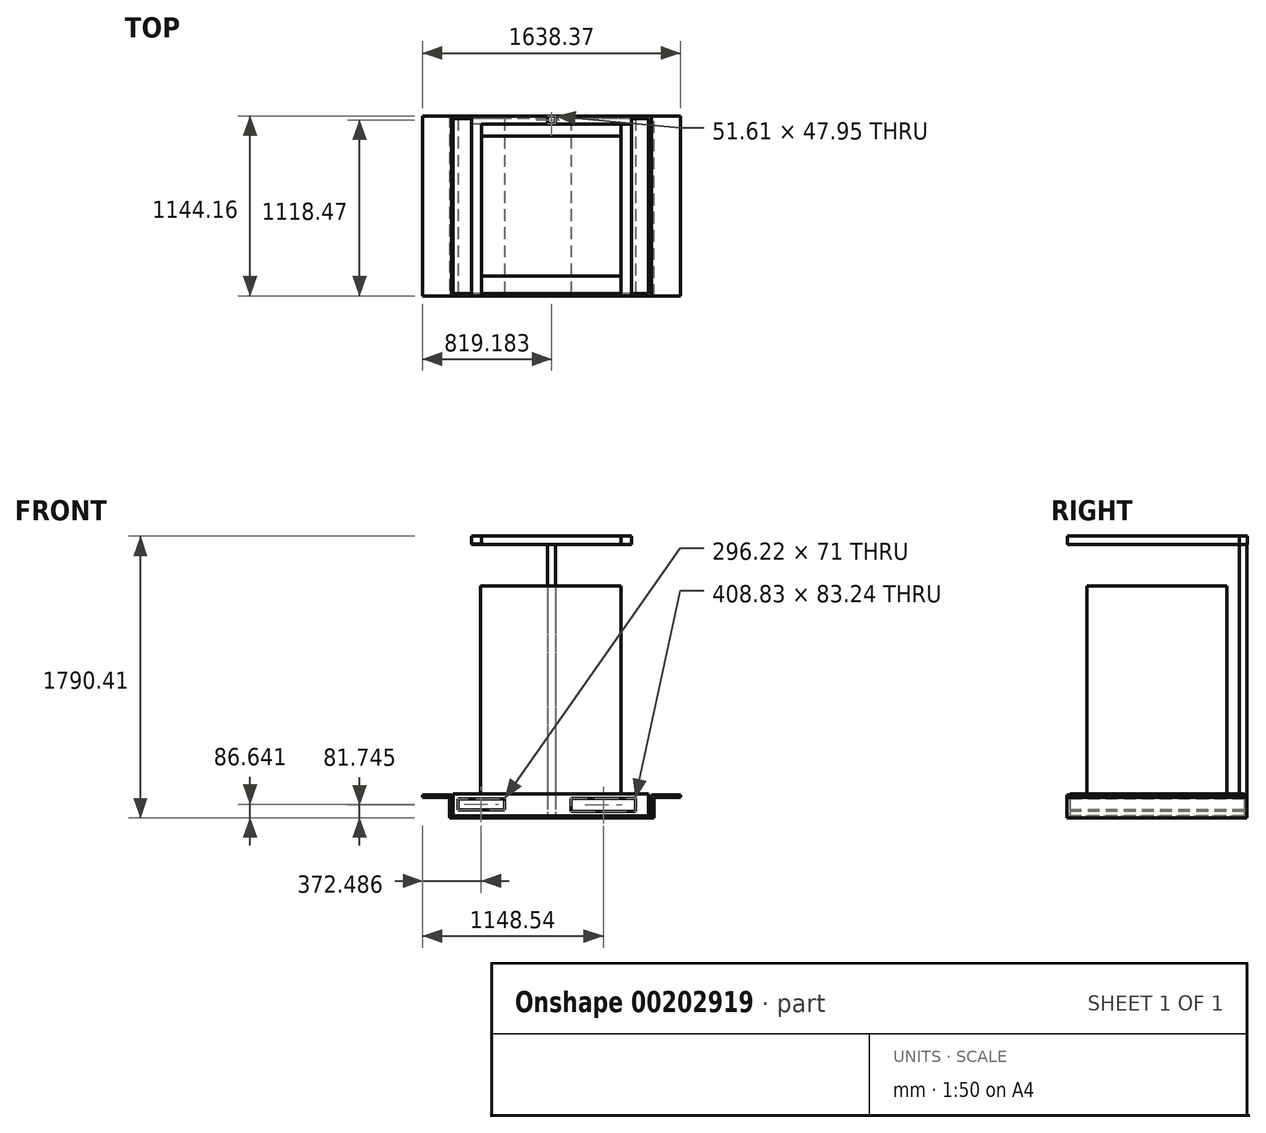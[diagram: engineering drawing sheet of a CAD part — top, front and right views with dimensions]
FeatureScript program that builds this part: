
annotation { "Feature Type Name" : "Feature", "Feature Type Description" : "" }
export const myFeature = defineFeature(function(context is Context, id is Id, definition is map)
    precondition{}
    {
        {
            var Q0;
            Q0=qCreatedBy(makeId("Front.planeOp"),FACE);
            var sketch = newSketch(context, id + "F0", { "sketchPlane" : qUnion([Q0])});
            skLineSegment(sketch, "E0.bottom", {"start": v(-65.9, -40.87) * mm, "end": v(1218.93, -40.87) * mm});
            skLineSegment(sketch, "E0.top", {"start": v(-65.9, -53.28) * mm, "end": v(1218.93, -53.28) * mm});
            skLineSegment(sketch, "E0.left", {"start": v(-65.9, -40.87) * mm, "end": v(-65.9, -53.28) * mm});
            skLineSegment(sketch, "E0.right", {"start": v(1218.93, -40.87) * mm, "end": v(1218.93, -53.28) * mm});
            skSolve(sketch);
        }
        {
            var Q0;
            Q0 = qSketchRegion(id + "F0", true);
            extrude(context, id + "F1", {"entities" : qUnion([Q0]), "endBound" : BoundingType.SYMMETRIC, "depth" : 1143 * mm});
        }
        {
            var Q0;
            Q0=makeQuery(id+"F1.opExtrude","CAP_FACE",FACE,{"disambiguationData":[OSD([sQuery(id+"F0.wireOp",EDGE,"E0.bottom"),sQuery(id+"F0.wireOp",EDGE,"E0.top"),sQuery(id+"F0.wireOp",EDGE,"E0.left"),sQuery(id+"F0.wireOp",EDGE,"E0.right")])],"isStart":false});
            var sketch = newSketch(context, id + "F2", { "sketchPlane" : qUnion([Q0])});
            skLineSegment(sketch, "E1", {"start": v(-65.9, -40.87) * mm, "end": v(-65.9, 93.39) * mm});
            skLineSegment(sketch, "E2", {"start": v(-65.9, 93.39) * mm, "end": v(-249.8, 93.39) * mm});
            skLineSegment(sketch, "E3", {"start": v(-249.8, 93.39) * mm, "end": v(-249.8, 77.85) * mm});
            skLineSegment(sketch, "E4", {"start": v(-65.9, -40.87) * mm, "end": v(-65.9, -53.28) * mm});
            skLineSegment(sketch, "E5", {"start": v(-65.9, -53.28) * mm, "end": v(-80.16, -53.28) * mm});
            skLineSegment(sketch, "E6", {"start": v(-80.16, -53.28) * mm, "end": v(-80.16, 77.85) * mm});
            skLineSegment(sketch, "E7", {"start": v(-249.8, 77.85) * mm, "end": v(-80.16, 77.85) * mm});
            skSolve(sketch);
        }
        {
            var Q0;
            Q0 = qSketchRegion(id + "F2", true);
            extrude(context, id + "F3", {"entities" : qUnion([Q0]), "operationType" : NewBodyOperationType.ADD, "oppositeDirection" : true, "depth" : 1143 * mm});
        }
        {
            var Q0;
            Q0=makeQuery(id+"F3.opExtrude","SWEPT_FACE",FACE,{"disambiguationData":[OSD([sQuery(id+"F2.wireOp",EDGE,"E6")])]});
            var Q1;
            Q1=makeQuery(id+"F1.opExtrude","SWEPT_FACE",FACE,{"disambiguationData":[OSD([sQuery(id+"F0.wireOp",EDGE,"E0.right")])]});
            cPlane(context, id + "F4", {"entities" : qUnion([Q0, Q1]), "cplaneType" : CPlaneType.MID_PLANE, "offset" : 25.4 * mm, "width" : 152.4 * mm, "height" : 152.4 * mm});
        }
        {
            var Q0;
            Q0=makeQuery(id+"F1.opExtrude","SWEPT_BODY",BODY,{"disambiguationData":[OSD([sQuery(id+"F0.wireOp",EDGE,"E0.bottom"),sQuery(id+"F0.wireOp",EDGE,"E0.top"),sQuery(id+"F0.wireOp",EDGE,"E0.left"),sQuery(id+"F0.wireOp",EDGE,"E0.right")])]});
            var Q1;
            Q1=qCreatedBy(id+"F4.planeOp",FACE);
            mirror(context, id + "F5", {"operationType" : NewBodyOperationType.ADD, "entities" : qUnion([Q0]), "mirrorPlane" : qUnion([Q1])});
        }
        {
            var Q0;
            Q0=makeQuery(id+"F1.opExtrude","SWEPT_FACE",FACE,{"disambiguationData":[OSD([sQuery(id+"F0.wireOp",EDGE,"E0.bottom")])]});
            var sketch = newSketch(context, id + "F6", { "sketchPlane" : qUnion([Q0])});
            skLineSegment(sketch, "E8.bottom", {"start": v(595.19, 570.95) * mm, "end": v(543.58, 570.95) * mm});
            skLineSegment(sketch, "E8.top", {"start": v(595.19, 523) * mm, "end": v(543.58, 523) * mm});
            skLineSegment(sketch, "E8.left", {"start": v(595.19, 570.95) * mm, "end": v(595.19, 523) * mm});
            skLineSegment(sketch, "E8.right", {"start": v(543.58, 570.95) * mm, "end": v(543.58, 523) * mm});
            skPoint(sketch, "E8.middle", {"position": v(569.38, 546.97) * mm});
            skSolve(sketch);
        }
        {
            var Q0;
            Q0 = qSketchRegion(id + "F6", true);
            extrude(context, id + "F7", {"entities" : qUnion([Q0]), "operationType" : NewBodyOperationType.ADD, "depth" : 1778 * mm});
        }
        {
            var Q0;
            Q0=qCreatedBy(id+"F4.planeOp",FACE);
            var sketch = newSketch(context, id + "F8", { "sketchPlane" : qUnion([Q0])});
            skLineSegment(sketch, "E9.bottom", {"start": v(-572.66, 1736.65) * mm, "end": v(-521.2, 1736.65) * mm});
            skLineSegment(sketch, "E9.top", {"start": v(-572.66, 1685.18) * mm, "end": v(-521.2, 1685.18) * mm});
            skLineSegment(sketch, "E9.left", {"start": v(-572.66, 1736.65) * mm, "end": v(-572.66, 1685.18) * mm});
            skLineSegment(sketch, "E9.right", {"start": v(-521.2, 1736.65) * mm, "end": v(-521.2, 1685.18) * mm});
            skPoint(sketch, "E9.middle", {"position": v(-546.93, 1710.91) * mm});
            skSolve(sketch);
        }
        {
            var Q0;
            Q0 = qSketchRegion(id + "F8", true);
            extrude(context, id + "F9", {"entities" : qUnion([Q0]), "operationType" : NewBodyOperationType.ADD, "endBound" : BoundingType.SYMMETRIC, "depth" : 1016 * mm});
        }
        {
            var Q0;
            Q0=makeQuery(id+"F9.opExtrude","SWEPT_FACE",FACE,{"disambiguationData":[OSD([sQuery(id+"F8.wireOp",EDGE,"E9.right")])]});
            var sketch = newSketch(context, id + "F10", { "sketchPlane" : qUnion([Q0])});
            skLineSegment(sketch, "E10.bottom", {"start": v(125.13, 1736.65) * mm, "end": v(61.48, 1736.65) * mm});
            skLineSegment(sketch, "E10.top", {"start": v(125.13, 1685.74) * mm, "end": v(61.48, 1685.74) * mm});
            skLineSegment(sketch, "E10.left", {"start": v(125.13, 1736.65) * mm, "end": v(125.13, 1685.74) * mm});
            skLineSegment(sketch, "E10.right", {"start": v(61.48, 1736.65) * mm, "end": v(61.48, 1685.74) * mm});
            skLineSegment(sketch, "E11.bottom", {"start": v(1076.3, 1736.46) * mm, "end": v(1010.24, 1736.46) * mm});
            skLineSegment(sketch, "E11.top", {"start": v(1076.3, 1684.97) * mm, "end": v(1010.24, 1684.97) * mm});
            skLineSegment(sketch, "E11.left", {"start": v(1076.3, 1736.46) * mm, "end": v(1076.3, 1684.97) * mm});
            skLineSegment(sketch, "E11.right", {"start": v(1010.24, 1736.46) * mm, "end": v(1010.24, 1684.97) * mm});
            skPoint(sketch, "E11.middle", {"position": v(1043.28, 1710.71) * mm});
            skSolve(sketch);
        }
        {
            var Q0;
            Q0 = qSketchRegion(id + "F10", true);
            extrude(context, id + "F11", {"entities" : qUnion([Q0]), "operationType" : NewBodyOperationType.ADD, "depth" : 1092.2 * mm});
        }
        {
            var Q0;
            Q0=makeQuery(id+"F1.opExtrude","SWEPT_FACE",FACE,{"disambiguationData":[OSD([sQuery(id+"F0.wireOp",EDGE,"E0.bottom")])]});
            var sketch = newSketch(context, id + "F12", { "sketchPlane" : qUnion([Q0])});
            skLineSegment(sketch, "E12.bottom", {"start": v(1185.44, 554.6) * mm, "end": v(-56.5, 554.6) * mm});
            skLineSegment(sketch, "E12.top", {"start": v(1185.44, -554.6) * mm, "end": v(-56.5, -554.6) * mm});
            skLineSegment(sketch, "E12.left", {"start": v(1185.44, 554.6) * mm, "end": v(1185.44, -554.6) * mm});
            skLineSegment(sketch, "E12.right", {"start": v(-56.5, 554.6) * mm, "end": v(-56.5, -554.6) * mm});
            skPoint(sketch, "E12.middle", {"position": v(564.47, 0) * mm});
            skSolve(sketch);
        }
        {
            var Q0;
            Q0 = qSketchRegion(id + "F12", true);
            extrude(context, id + "F13", {"entities" : qUnion([Q0]), "operationType" : NewBodyOperationType.ADD, "depth" : 139.7 * mm});
        }
        {
            var Q0;
            Q0=makeQuery(id+"F13.opExtrude","SWEPT_FACE",FACE,{"disambiguationData":[OSD([sQuery(id+"F12.wireOp",EDGE,"E12.top")])]});
            var sketch = newSketch(context, id + "F14", { "sketchPlane" : qUnion([Q0])});
            skLineSegment(sketch, "E13.bottom", {"start": v(270.8, 68.86) * mm, "end": v(-25.42, 68.86) * mm});
            skLineSegment(sketch, "E13.top", {"start": v(270.8, -2.14) * mm, "end": v(-25.42, -2.14) * mm});
            skLineSegment(sketch, "E13.left", {"start": v(270.8, 68.86) * mm, "end": v(270.8, -2.14) * mm});
            skLineSegment(sketch, "E13.right", {"start": v(-25.42, 68.86) * mm, "end": v(-25.42, -2.14) * mm});
            skPoint(sketch, "E13.middle", {"position": v(122.69, 33.36) * mm});
            skLineSegment(sketch, "E14.bottom", {"start": v(1103.15, 70.08) * mm, "end": v(694.32, 70.08) * mm});
            skLineSegment(sketch, "E14.top", {"start": v(1103.15, -13.15) * mm, "end": v(694.32, -13.15) * mm});
            skLineSegment(sketch, "E14.left", {"start": v(1103.15, 70.08) * mm, "end": v(1103.15, -13.15) * mm});
            skLineSegment(sketch, "E14.right", {"start": v(694.32, 70.08) * mm, "end": v(694.32, -13.15) * mm});
            skPoint(sketch, "E14.middle", {"position": v(898.73, 28.46) * mm});
            skSolve(sketch);
        }
        {
            var Q0;
            Q0 = qSketchRegion(id + "F14", true);
            extrude(context, id + "F15", {"entities" : qUnion([Q0]), "operationType" : NewBodyOperationType.REMOVE, "endBound" : BoundingType.THROUGH_ALL, "oppositeDirection" : true, "depth" : 25.4 * mm});
        }
        {
            var Q0;
            Q0=makeQuery(id+"F13.opExtrude","CAP_FACE",FACE,{"disambiguationData":[OSD([sQuery(id+"F12.wireOp",EDGE,"E12.bottom"),sQuery(id+"F12.wireOp",EDGE,"E12.top"),sQuery(id+"F12.wireOp",EDGE,"E12.left"),sQuery(id+"F12.wireOp",EDGE,"E12.right")])],"isStart":false});
            var sketch = newSketch(context, id + "F16", { "sketchPlane" : qUnion([Q0])});
            skLineSegment(sketch, "E15.bottom", {"start": v(1011.76, 444.83) * mm, "end": v(117.18, 444.83) * mm});
            skLineSegment(sketch, "E15.top", {"start": v(1011.76, -444.83) * mm, "end": v(117.18, -444.83) * mm});
            skLineSegment(sketch, "E15.left", {"start": v(1011.76, 444.83) * mm, "end": v(1011.76, -444.83) * mm});
            skLineSegment(sketch, "E15.right", {"start": v(117.18, 444.83) * mm, "end": v(117.18, -444.83) * mm});
            skPoint(sketch, "E15.middle", {"position": v(564.47, 0) * mm});
            skSolve(sketch);
        }
        {
            var Q0;
            Q0 = qSketchRegion(id + "F16", true);
            extrude(context, id + "F17", {"entities" : qUnion([Q0]), "operationType" : NewBodyOperationType.ADD, "depth" : 1320.8 * mm});
        }
    });
